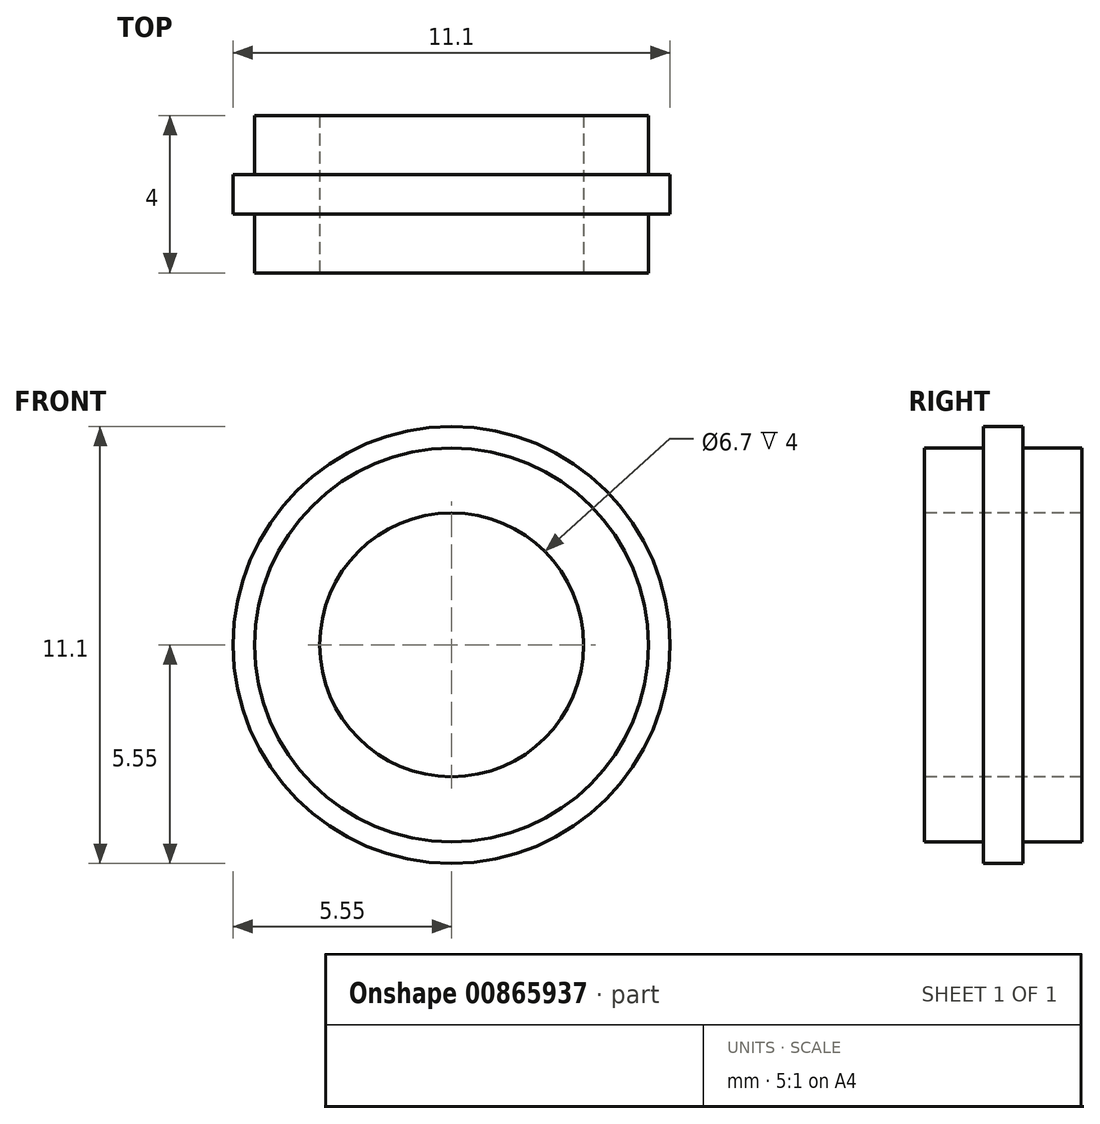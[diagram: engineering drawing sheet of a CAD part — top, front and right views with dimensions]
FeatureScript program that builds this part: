
annotation { "Feature Type Name" : "Feature", "Feature Type Description" : "" }
export const myFeature = defineFeature(function(context is Context, id is Id, definition is map)
    precondition{}
    {
        {
            var Q0;
            Q0=qCreatedBy(makeId("Right.planeOp"),FACE);
            var sketch = newSketch(context, id + "F0", { "sketchPlane" : qUnion([Q0])});
            skLineSegment(sketch, "E0", {"start": v(-4.5, 0) * mm, "end": v(4.5, 0) * mm, "construction": true});
            skLineSegment(sketch, "E1", {"start": v(-2, 3.35) * mm, "end": v(-2, 5) * mm});
            skLineSegment(sketch, "E2", {"start": v(-2, 5) * mm, "end": v(-0.5, 5) * mm});
            skLineSegment(sketch, "E3", {"start": v(-0.5, 5) * mm, "end": v(-0.5, 5.55) * mm});
            skLineSegment(sketch, "E4", {"start": v(-0.5, 5.55) * mm, "end": v(0.5, 5.55) * mm});
            skLineSegment(sketch, "E5", {"start": v(0.5, 5.55) * mm, "end": v(0.5, 5) * mm});
            skLineSegment(sketch, "E6", {"start": v(0.5, 5) * mm, "end": v(2, 5) * mm});
            skLineSegment(sketch, "E7", {"start": v(2, 5) * mm, "end": v(2, 3.35) * mm});
            skLineSegment(sketch, "E8", {"start": v(-2, 3.35) * mm, "end": v(2, 3.35) * mm});
            skSolve(sketch);
        }
        {
            var Q0;
            Q0 = qSketchRegion(id + "F0", true);
            var Q1;
            Q1=sQuery(id+"F0.wireOp",EDGE,"E0");
            revolve(context, id + "F1", {"surfaceOperationType" : NewSurfaceOperationType.NEW, "entities" : qUnion([Q0]), "axis" : qUnion([Q1]), "revolveType" : RevolveType.FULL});
        }
    });
